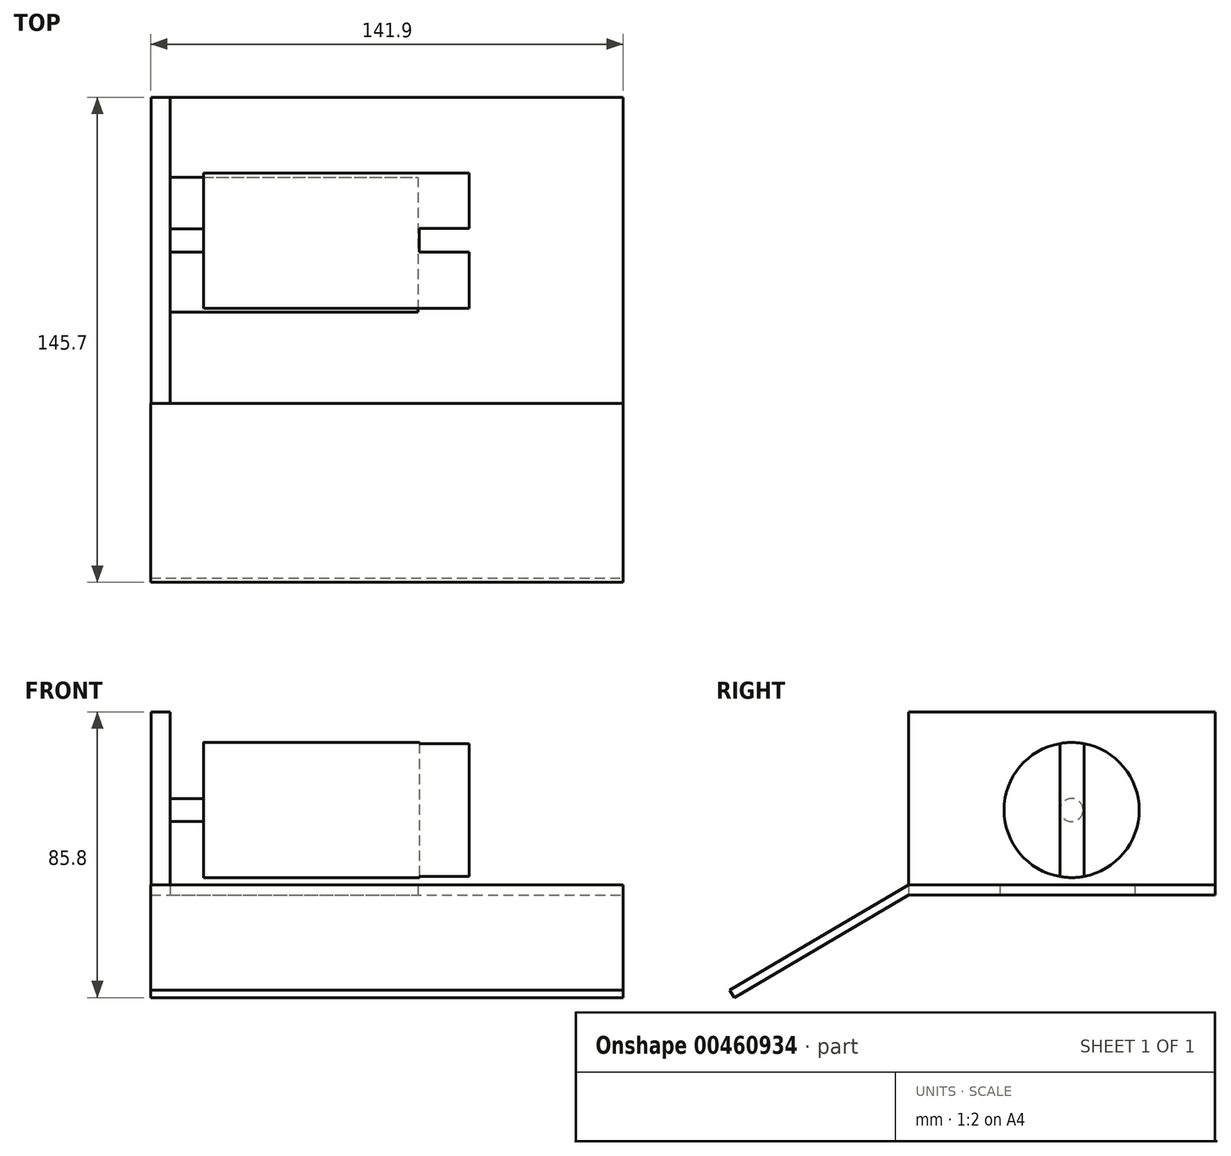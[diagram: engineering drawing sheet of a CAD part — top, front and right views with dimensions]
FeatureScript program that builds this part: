
annotation { "Feature Type Name" : "Feature", "Feature Type Description" : "" }
export const myFeature = defineFeature(function(context is Context, id is Id, definition is map)
    precondition{}
    {
        {
            var Q0;
            Q0=qCreatedBy(makeId("Top.planeOp"),FACE);
            var sketch = newSketch(context, id + "F0", { "sketchPlane" : qUnion([Q0])});
            skLineSegment(sketch, "E0.bottom", {"start": v(-34.87, 15.34) * mm, "end": v(39.5, 15.34) * mm});
            skLineSegment(sketch, "E0.top", {"start": v(-34.87, -25.18) * mm, "end": v(39.5, -25.18) * mm});
            skLineSegment(sketch, "E0.left", {"start": v(-34.87, 15.34) * mm, "end": v(-34.87, -25.18) * mm});
            skLineSegment(sketch, "E0.right", {"start": v(39.5, 15.34) * mm, "end": v(39.5, -25.18) * mm});
            skLineSegment(sketch, "E1.bottom", {"start": v(-34.87, 39.36) * mm, "end": v(101.15, 39.36) * mm});
            skLineSegment(sketch, "E1.top", {"start": v(-34.87, -52.67) * mm, "end": v(101.15, -52.67) * mm});
            skLineSegment(sketch, "E1.left", {"start": v(-34.87, 39.36) * mm, "end": v(-34.87, -52.67) * mm});
            skLineSegment(sketch, "E1.right", {"start": v(101.15, 39.36) * mm, "end": v(101.15, -52.67) * mm});
            skLineSegment(sketch, "E2.bottom", {"start": v(-34.87, 39.36) * mm, "end": v(-40.66, 39.36) * mm});
            skLineSegment(sketch, "E2.top", {"start": v(-34.87, -52.67) * mm, "end": v(-40.66, -52.67) * mm});
            skLineSegment(sketch, "E2.right", {"start": v(-40.66, 39.36) * mm, "end": v(-40.66, -52.67) * mm});
            skSolve(sketch);
        }
        {
            var Q0;
            {var subQ2=sQuery(id+"F0.wireOp",EDGE,"E0.bottom");Q0=makeQuery(id+"F0.imprint","IMPRINT",FACE,{"disambiguationData":[TD([[makeQuery(id+"F0.imprint","IMPRINT",EDGE,{"derivedFrom":subQ2}),1.0]])]});}
            extrude(context, id + "F1", {"entities" : qUnion([Q0]), "depth" : 3 * mm, "offsetDistance" : 25 * mm});
        }
        {
            var Q0;
            {var subQ3=sQuery(id+"F0.wireOp",EDGE,"E2.bottom");Q0=makeQuery(id+"F0.imprint","IMPRINT",FACE,{"disambiguationData":[TD([[makeQuery(id+"F0.imprint","IMPRINT",EDGE,{"derivedFrom":subQ3}),1.0]])]});}
            extrude(context, id + "F2", {"entities" : qUnion([Q0]), "operationType" : NewBodyOperationType.ADD, "depth" : 55 * mm, "offsetDistance" : 25 * mm});
        }
        {
            var Q0;
            Q0=makeQuery(id+"F2.opExtrude","SWEPT_FACE",FACE,{"disambiguationData":[OSD([sQuery(id+"F0.wireOp",EDGE,"E1.left")])]});
            var sketch = newSketch(context, id + "F3", { "sketchPlane" : qUnion([Q0])});
            skCircle(sketch, "E3", {"center": v(-3.7, 25.54) * mm, "radius": 3.47 * mm});
            skSolve(sketch);
        }
        {
            var Q0;
            Q0=makeQuery(id+"F3.imprint","IMPRINT",FACE,{"disambiguationData":[TD([[makeQuery(id+"F3.imprint","IMPRINT",EDGE,{"derivedFrom":sQuery(id+"F3.wireOp",EDGE,"E3")}),1.0]])]});
            extrude(context, id + "F4", {"entities" : qUnion([Q0]), "operationType" : NewBodyOperationType.ADD, "depth" : 10 * mm, "offsetDistance" : 25 * mm});
        }
        {
            var Q0;
            Q0=makeQuery(id+"F1.opExtrude","SWEPT_FACE",FACE,{"disambiguationData":[OSD([sQuery(id+"F0.wireOp",EDGE,"E1.right")])]});
            var sketch = newSketch(context, id + "F5", { "sketchPlane" : qUnion([Q0])});
            skLineSegment(sketch, "E4", {"start": v(-52.67, 0) * mm, "end": v(-105.03, -30.8) * mm});
            skLineSegment(sketch, "E5", {"start": v(-105.03, -30.8) * mm, "end": v(-106.34, -28.57) * mm});
            skLineSegment(sketch, "E6", {"start": v(-106.34, -28.57) * mm, "end": v(-52.67, 3) * mm});
            skSolve(sketch);
        }
        {
            var Q0;
            Q0=makeQuery(id+"F5.imprint","IMPRINT",FACE,{"disambiguationData":[TD([[makeQuery(id+"F5.imprint","IMPRINT",EDGE,{"derivedFrom":sQuery(id+"F5.wireOp",EDGE,"E4")}),-1.0]])]});
            extrude(context, id + "F6", {"entities" : qUnion([Q0]), "operationType" : NewBodyOperationType.ADD, "oppositeDirection" : true, "depth" : 141.9 * mm, "offsetDistance" : 25 * mm});
        }
        {
            var Q0;
            Q0=makeQuery(id+"F4.opExtrude","CAP_FACE",FACE,{"disambiguationData":[OSD([sQuery(id+"F3.wireOp",EDGE,"E3")])],"isStart":false});
            var sketch = newSketch(context, id + "F7", { "sketchPlane" : qUnion([Q0])});
            skCircle(sketch, "E7", {"center": v(-3.7, 25.54) * mm, "radius": 20.3 * mm});
            skSolve(sketch);
        }
        {
            var Q0;
            Q0=makeQuery(id+"F7.imprint","IMPRINT",FACE,{"disambiguationData":[TD([[makeQuery(id+"F7.imprint","IMPRINT",EDGE,{"derivedFrom":sQuery(id+"F7.wireOp",EDGE,"E7")}),1.0]])]});
            var Q1;
            Q1=makeQuery(id+"F7.imprint","IMPRINT",FACE,{"disambiguationData":[TD([[makeQuery(id+"F7.imprint","IMPRINT",EDGE,{"derivedFrom":makeQuery(id+"F4.opExtrude","CAP_EDGE",EDGE,{"disambiguationData":[OSD([sQuery(id+"F3.wireOp",EDGE,"E3")])],"isStart":false})}),1.0]])]});
            extrude(context, id + "F8", {"entities" : qUnion([Q0, Q1]), "depth" : 64.8 * mm, "offsetDistance" : 25 * mm});
        }
        {
            var Q0;
            Q0=makeQuery(id+"F8.opExtrude","CAP_FACE",FACE,{"disambiguationData":[OSD([sQuery(id+"F7.wireOp",EDGE,"E7")])],"isStart":false});
            var sketch = newSketch(context, id + "F9", { "sketchPlane" : qUnion([Q0])});
            skArc(sketch, "E8", {"start": v(-7.17, 45.56) * mm, "mid": v(-24.02, 25.54) * mm, "end": v(-7.17, 5.52) * mm});
            skLineSegment(sketch, "E9.left", {"start": v(-7.17, 45.56) * mm, "end": v(-7.17, 5.52) * mm});
            skLineSegment(sketch, "E9.right", {"start": v(0, 45.52) * mm, "end": v(0, 5.57) * mm});
            skArc(sketch, "E10.trimOffspring", {"start": v(0, 5.57) * mm, "mid": v(16.61, 25.54) * mm, "end": v(0, 45.52) * mm});
            skPoint(sketch, "E11.orphan", {"position": v(0, 3.61) * mm});
            skSolve(sketch);
        }
        {
            var Q0;
            {var subQ0=sQuery(id+"F9.wireOp",EDGE,"E9.left");var subQ1=makeQuery(id+"F8.opExtrude","CAP_EDGE",EDGE,{"disambiguationData":[OSD([sQuery(id+"F7.wireOp",EDGE,"E7")])],"isStart":false});var subQ2=makeQuery(id+"F9.imprint","INTERSECT",VERTEX,{"disambiguationData":[OD(0.0)],"derivedFrom":[subQ1,subQ0]});Q0=makeQuery(id+"F9.imprint","IMPRINT",FACE,{"disambiguationData":[TD([[makeQuery(id+"F9.imprint","IMPRINT",EDGE,{"disambiguationData":[TD([[subQ2,-1.0]])],"derivedFrom":subQ0}),-1.0]])]});}
            var Q1;
            {var subQ0=sQuery(id+"F9.wireOp",EDGE,"E9.right");var subQ1=makeQuery(id+"F8.opExtrude","CAP_EDGE",EDGE,{"disambiguationData":[OSD([sQuery(id+"F7.wireOp",EDGE,"E7")])],"isStart":false});var subQ2=makeQuery(id+"F9.imprint","INTERSECT",VERTEX,{"disambiguationData":[OD(0.0)],"derivedFrom":[subQ1,subQ0]});Q1=makeQuery(id+"F9.imprint","IMPRINT",FACE,{"disambiguationData":[TD([[makeQuery(id+"F9.imprint","IMPRINT",EDGE,{"disambiguationData":[TD([[subQ2,-1.0]])],"derivedFrom":subQ0}),1.0]])]});}
            extrude(context, id + "F10", {"entities" : qUnion([Q0, Q1]), "operationType" : NewBodyOperationType.ADD, "depth" : 15 * mm, "offsetDistance" : 25 * mm});
        }
    });
